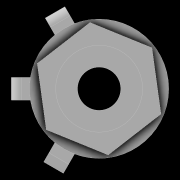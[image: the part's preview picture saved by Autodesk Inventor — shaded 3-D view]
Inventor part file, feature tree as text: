
AUTODESK INVENTOR PART (.ipt)
format: ipt  version: 2020 (Build 240168000, 168)  size: 288,768 bytes
history: native  units: in
note: dims shown in document units (in); Inventor stores cm internally (conversion verified against a paired STEP export)
features: sketch x10, extrude x9, other x4, fillet x1, thread x1
ambient origin geometry x8: Origin, YZ Plane, XZ Plane, XY Plane, X Axis, Y Axis, Z Axis, Center Point
bodies: Body1 (feature_tree)
feature tree (25):
  other  "Fishman1/4Jack"
  extrude  "FishmanJackBodyFeature"  Depth=0.13in
  extrude  "FishmanJackLegsFeature"  Depth=0.4in
  fillet  "FishmanJackLegFilletsFeature"  Radius=0.05in
  extrude  "Extrusion10"  Depth=0.05in
  extrude  "Extrusion11"  Depth=0.05in
  extrude  "Extrusion12"  Depth=0.05in
  extrude  "Extrusion13"  Depth=0.05in TaperAngle=0.0deg
  extrude  "Extrusion14"  Depth=0.5in
  extrude  "Extrusion15"  Depth=0.1in TaperAngle=0.0deg
  extrude  "Extrusion16"  TaperAngle=0.0deg  [1 undecoded]
  other  "Bend Part1"
  other  "Bend Part2"
  other  "Bend Part3"
  thread  "Thread1"  [1 undecoded]
  sketch  "Sketch15"  dims[d37=0.8in d38=60.0deg d39=60.0deg d60=0.7in d61=0.13in]
  sketch  "Sketch16"  dims[d62=0.25in d63=0.4in d125=0.05in d126=0.0in]
  sketch  "Sketch17"  dims[d127=0.05in d128=0.0in d129=0.05in]
  sketch  "Sketch18"  dims[d130=0.05in d131=0.05in]
  sketch  "Sketch19"  dims[d132=0.05in d133=0.05in]
  sketch  "Sketch20"  dims[d134=0.5in d135=0.05in d136=0.0in]
  sketch  "Sketch21"  dims[d137=0.05in d138=0.0in d139=0.5in]
  sketch  "Sketch22"  dims[d140=0.05in d141=0.0in d142=0.1in d143=0.0in]
  sketch  "Sketch23"  dims[d144=0.25in d145=0.0in d146=0.0in d147=0.3333in]
  sketch  "Sketch24"  dims[d148=0.1in d149=0.0in d150=0.5in d151=0.25in d152=0.0in d153=0.0519in d154=0.06in d155=90.0deg d156=0.05in d157=0.06in d158=90.0deg d159=0.1867in d160=0.06in d161=90.0deg d162=0.25in d163=0.0in]
note: 2 required parameter values undecoded (feature->parameter linkage not recoverable at this tier; creation-order binding heuristic only, values carry confidence <= 0.55)
